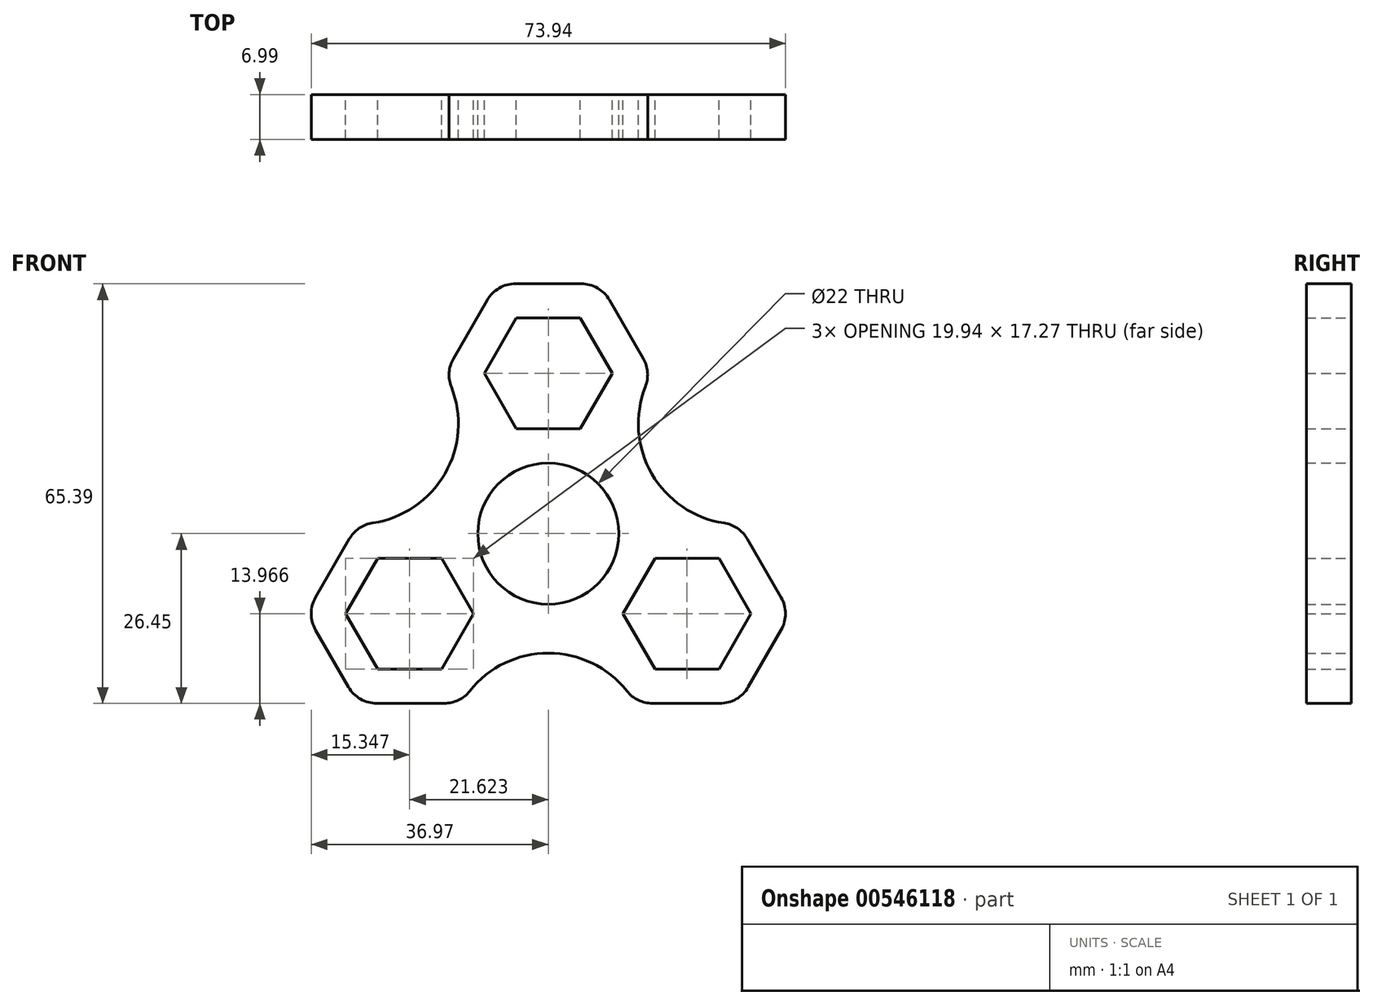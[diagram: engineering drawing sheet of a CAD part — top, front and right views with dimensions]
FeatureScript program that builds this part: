
annotation { "Feature Type Name" : "Feature", "Feature Type Description" : "" }
export const myFeature = defineFeature(function(context is Context, id is Id, definition is map)
    precondition{}
    {
        {
            var Q0;
            Q0=qCreatedBy(makeId("Front.planeOp"),FACE);
            var sketch = newSketch(context, id + "F0", { "sketchPlane" : qUnion([Q0])});
            skCircle(sketch, "E0", {"center": v(0, 0) * mm, "radius": 11 * mm});
            skCircle(sketch, "E1.cCircle", {"center": v(0, 0) * mm, "radius": 17.3 * mm, "construction": true});
            skLineSegment(sketch, "E1.0", {"start": v(-9.99, 17.3) * mm, "end": v(9.99, 17.3) * mm});
            skLineSegment(sketch, "E1.1", {"start": v(9.99, 17.3) * mm, "end": v(19.98, 0) * mm});
            skLineSegment(sketch, "E1.2", {"start": v(19.98, 0) * mm, "end": v(9.99, -17.3) * mm});
            skLineSegment(sketch, "E1.3", {"start": v(9.99, -17.3) * mm, "end": v(-9.99, -17.3) * mm});
            skLineSegment(sketch, "E1.4", {"start": v(-9.99, -17.3) * mm, "end": v(-19.98, 0) * mm});
            skLineSegment(sketch, "E1.5", {"start": v(-19.98, 0) * mm, "end": v(-9.99, 17.3) * mm});
            skPoint(sketch, "E1.0.midPoint", {"position": v(0, 17.3) * mm});
            skCircle(sketch, "E2.cCircle", {"center": v(0, 24.97) * mm, "radius": 13.97 * mm, "construction": true});
            skLineSegment(sketch, "E2.0", {"start": v(8.07, 11) * mm, "end": v(-8.07, 11) * mm});
            skLineSegment(sketch, "E2.1", {"start": v(-8.07, 11) * mm, "end": v(-16.13, 24.97) * mm});
            skLineSegment(sketch, "E2.2", {"start": v(-16.13, 24.97) * mm, "end": v(-8.07, 38.94) * mm});
            skLineSegment(sketch, "E2.3", {"start": v(-8.07, 38.94) * mm, "end": v(8.07, 38.94) * mm});
            skLineSegment(sketch, "E2.4", {"start": v(8.07, 38.94) * mm, "end": v(16.13, 24.97) * mm});
            skLineSegment(sketch, "E2.5", {"start": v(16.13, 24.97) * mm, "end": v(8.07, 11) * mm});
            skPoint(sketch, "E2.0.midPoint", {"position": v(0, 11) * mm});
            skCircle(sketch, "E3.cCircle", {"center": v(0, 24.97) * mm, "radius": 8.64 * mm, "construction": true});
            skLineSegment(sketch, "E3.0", {"start": v(-4.99, 33.6) * mm, "end": v(4.99, 33.6) * mm});
            skLineSegment(sketch, "E3.1", {"start": v(4.99, 33.6) * mm, "end": v(9.97, 24.97) * mm});
            skLineSegment(sketch, "E3.2", {"start": v(9.97, 24.97) * mm, "end": v(4.99, 16.33) * mm});
            skLineSegment(sketch, "E3.3", {"start": v(4.99, 16.33) * mm, "end": v(-4.99, 16.33) * mm});
            skLineSegment(sketch, "E3.4", {"start": v(-4.99, 16.33) * mm, "end": v(-9.97, 24.97) * mm});
            skLineSegment(sketch, "E3.5", {"start": v(-9.97, 24.97) * mm, "end": v(-4.99, 33.6) * mm});
            skPoint(sketch, "E3.0.midPoint", {"position": v(0, 33.6) * mm});
            skCircle(sketch, "E4.1.0", {"center": v(-21.62, -12.48) * mm, "radius": 13.97 * mm, "construction": true});
            skCircle(sketch, "E4.1.1", {"center": v(-21.62, -12.48) * mm, "radius": 8.64 * mm, "construction": true});
            skLineSegment(sketch, "E4.1.2", {"start": v(-16.64, -21.12) * mm, "end": v(-26.6, -21.12) * mm});
            skLineSegment(sketch, "E4.1.3", {"start": v(-13.56, -26.45) * mm, "end": v(-29.69, -26.45) * mm});
            skLineSegment(sketch, "E4.1.4", {"start": v(-29.69, -26.45) * mm, "end": v(-37.75, -12.48) * mm});
            skLineSegment(sketch, "E4.1.5", {"start": v(-13.56, 1.49) * mm, "end": v(-5.5, -12.48) * mm});
            skLineSegment(sketch, "E4.1.6", {"start": v(-16.64, -3.85) * mm, "end": v(-11.65, -12.48) * mm});
            skLineSegment(sketch, "E4.1.7", {"start": v(-11.65, -12.48) * mm, "end": v(-16.64, -21.12) * mm});
            skLineSegment(sketch, "E4.1.8", {"start": v(-26.6, -3.85) * mm, "end": v(-16.64, -3.85) * mm});
            skLineSegment(sketch, "E4.1.9", {"start": v(-31.6, -12.48) * mm, "end": v(-26.6, -3.85) * mm});
            skLineSegment(sketch, "E4.1.10", {"start": v(-29.69, 1.49) * mm, "end": v(-13.56, 1.49) * mm});
            skLineSegment(sketch, "E4.1.11", {"start": v(-37.75, -12.48) * mm, "end": v(-29.69, 1.49) * mm});
            skLineSegment(sketch, "E4.1.12", {"start": v(-5.5, -12.48) * mm, "end": v(-13.56, -26.45) * mm});
            skLineSegment(sketch, "E4.1.13", {"start": v(-26.6, -21.12) * mm, "end": v(-31.6, -12.48) * mm});
            skCircle(sketch, "E4.2.0", {"center": v(21.62, -12.48) * mm, "radius": 13.97 * mm, "construction": true});
            skCircle(sketch, "E4.2.1", {"center": v(21.62, -12.48) * mm, "radius": 8.64 * mm, "construction": true});
            skLineSegment(sketch, "E4.2.2", {"start": v(26.6, -3.85) * mm, "end": v(31.6, -12.48) * mm});
            skLineSegment(sketch, "E4.2.3", {"start": v(29.69, 1.49) * mm, "end": v(37.75, -12.48) * mm});
            skLineSegment(sketch, "E4.2.4", {"start": v(37.75, -12.48) * mm, "end": v(29.69, -26.45) * mm});
            skLineSegment(sketch, "E4.2.5", {"start": v(5.5, -12.48) * mm, "end": v(13.56, 1.49) * mm});
            skLineSegment(sketch, "E4.2.6", {"start": v(11.65, -12.48) * mm, "end": v(16.64, -3.85) * mm});
            skLineSegment(sketch, "E4.2.7", {"start": v(16.64, -3.85) * mm, "end": v(26.6, -3.85) * mm});
            skLineSegment(sketch, "E4.2.8", {"start": v(16.64, -21.12) * mm, "end": v(11.65, -12.48) * mm});
            skLineSegment(sketch, "E4.2.9", {"start": v(26.6, -21.12) * mm, "end": v(16.64, -21.12) * mm});
            skLineSegment(sketch, "E4.2.10", {"start": v(13.56, -26.45) * mm, "end": v(5.5, -12.48) * mm});
            skLineSegment(sketch, "E4.2.11", {"start": v(29.69, -26.45) * mm, "end": v(13.56, -26.45) * mm});
            skLineSegment(sketch, "E4.2.12", {"start": v(13.56, 1.49) * mm, "end": v(29.69, 1.49) * mm});
            skLineSegment(sketch, "E4.2.13", {"start": v(31.6, -12.48) * mm, "end": v(26.6, -21.12) * mm});
            skArc(sketch, "E5", {"start": v(-29.69, 1.49) * mm, "mid": v(-16.13, 9.31) * mm, "end": v(-16.13, 24.97) * mm});
            skArc(sketch, "E6", {"start": v(13.56, -26.45) * mm, "mid": v(0, -18.63) * mm, "end": v(-13.56, -26.45) * mm});
            skArc(sketch, "E7", {"start": v(16.13, 24.97) * mm, "mid": v(16.13, 9.31) * mm, "end": v(29.69, 1.49) * mm});
            skSolve(sketch);
        }
        {
            var Q0;
            Q0 = qSketchRegion(id + "F0", true);
            var Q1;
            {var subQ1=sQuery(id+"F0.wireOp",EDGE,"E2.0");var subQ7=sQuery(id+"F0.wireOp",EDGE,"E0");var subQ8=makeQuery(id+"F0.imprint","INTERSECT",VERTEX,{"derivedFrom":[subQ7,subQ1]});Q1=makeQuery(id+"F0.imprint","IMPRINT",FACE,{"disambiguationData":[TD([[makeQuery(id+"F0.imprint","IMPRINT",EDGE,{"disambiguationData":[TD([[subQ8,1.0]])],"derivedFrom":subQ7}),-1.0]])]});}
            var Q2;
            {var subQ1=sQuery(id+"F0.wireOp",EDGE,"E4.1.6");Q2=makeQuery(id+"F0.imprint","IMPRINT",FACE,{"disambiguationData":[TD([[makeQuery(id+"F0.imprint","IMPRINT",EDGE,{"derivedFrom":subQ1}),1.0]])]});}
            var Q3;
            {var subQ5=sQuery(id+"F0.wireOp",EDGE,"E0");var subQ7=sQuery(id+"F0.wireOp",EDGE,"E4.1.5");var subQ8=makeQuery(id+"F0.imprint","INTERSECT",VERTEX,{"derivedFrom":[subQ5,subQ7]});Q3=makeQuery(id+"F0.imprint","IMPRINT",FACE,{"disambiguationData":[TD([[makeQuery(id+"F0.imprint","IMPRINT",EDGE,{"disambiguationData":[TD([[subQ8,1.0]])],"derivedFrom":subQ5}),-1.0]])]});}
            var Q4;
            {var subQ1=sQuery(id+"F0.wireOp",EDGE,"E4.2.6");Q4=makeQuery(id+"F0.imprint","IMPRINT",FACE,{"disambiguationData":[TD([[makeQuery(id+"F0.imprint","IMPRINT",EDGE,{"derivedFrom":subQ1}),1.0]])]});}
            var Q5;
            {var subQ7=sQuery(id+"F0.wireOp",EDGE,"E3.3");Q5=makeQuery(id+"F0.imprint","IMPRINT",FACE,{"disambiguationData":[TD([[makeQuery(id+"F0.imprint","IMPRINT",EDGE,{"derivedFrom":subQ7}),1.0]])]});}
            var Q6;
            {var subQ1=sQuery(id+"F0.wireOp",EDGE,"E4.1.5");var subQ5=sQuery(id+"F0.wireOp",EDGE,"E0");var subQ6=makeQuery(id+"F0.imprint","INTERSECT",VERTEX,{"derivedFrom":[subQ5,subQ1]});Q6=makeQuery(id+"F0.imprint","IMPRINT",FACE,{"disambiguationData":[TD([[makeQuery(id+"F0.imprint","IMPRINT",EDGE,{"disambiguationData":[TD([[subQ6,-1.0]])],"derivedFrom":subQ5}),-1.0]])]});}
            extrude(context, id + "F1", {"entities" : qUnion([Q0, Q1, Q2, Q3, Q4, Q5, Q6]), "depth" : 7 * mm, "offsetDistance" : 25.4 * mm});
        }
        {
            var Q0;
            Q0=makeQuery(id+"F1.opExtrude","SWEPT_EDGE",EDGE,{"disambiguationData":[OSD([sQuery(id+"F0.wireOp",EDGE,"E2.4"),sQuery(id+"F0.wireOp",EDGE,"E2.5"),sQuery(id+"F0.wireOp",EDGE,"E7")])]});
            var Q1;
            Q1=makeQuery(id+"F1.opExtrude","SWEPT_EDGE",EDGE,{"disambiguationData":[OSD([sQuery(id+"F0.wireOp",EDGE,"E2.2"),sQuery(id+"F0.wireOp",EDGE,"E2.3")])]});
            var Q2;
            Q2=makeQuery(id+"F1.opExtrude","SWEPT_EDGE",EDGE,{"disambiguationData":[OSD([sQuery(id+"F0.wireOp",EDGE,"E2.3"),sQuery(id+"F0.wireOp",EDGE,"E2.4")])]});
            var Q3;
            Q3=makeQuery(id+"F1.opExtrude","SWEPT_EDGE",EDGE,{"disambiguationData":[OSD([sQuery(id+"F0.wireOp",EDGE,"E2.1"),sQuery(id+"F0.wireOp",EDGE,"E2.2"),sQuery(id+"F0.wireOp",EDGE,"E5")])]});
            var Q4;
            Q4=makeQuery(id+"F1.opExtrude","SWEPT_EDGE",EDGE,{"disambiguationData":[OSD([sQuery(id+"F0.wireOp",EDGE,"E4.1.10"),sQuery(id+"F0.wireOp",EDGE,"E4.1.11"),sQuery(id+"F0.wireOp",EDGE,"E5")])]});
            var Q5;
            Q5=makeQuery(id+"F1.opExtrude","SWEPT_EDGE",EDGE,{"disambiguationData":[OSD([sQuery(id+"F0.wireOp",EDGE,"E4.1.4"),sQuery(id+"F0.wireOp",EDGE,"E4.1.11")])]});
            var Q6;
            Q6=makeQuery(id+"F1.opExtrude","SWEPT_EDGE",EDGE,{"disambiguationData":[OSD([sQuery(id+"F0.wireOp",EDGE,"E4.1.3"),sQuery(id+"F0.wireOp",EDGE,"E4.1.12"),sQuery(id+"F0.wireOp",EDGE,"E6")])]});
            var Q7;
            Q7=makeQuery(id+"F1.opExtrude","SWEPT_EDGE",EDGE,{"disambiguationData":[OSD([sQuery(id+"F0.wireOp",EDGE,"E4.1.3"),sQuery(id+"F0.wireOp",EDGE,"E4.1.4")])]});
            var Q8;
            Q8=makeQuery(id+"F1.opExtrude","SWEPT_EDGE",EDGE,{"disambiguationData":[OSD([sQuery(id+"F0.wireOp",EDGE,"E4.2.10"),sQuery(id+"F0.wireOp",EDGE,"E4.2.11"),sQuery(id+"F0.wireOp",EDGE,"E6")])]});
            var Q9;
            Q9=makeQuery(id+"F1.opExtrude","SWEPT_EDGE",EDGE,{"disambiguationData":[OSD([sQuery(id+"F0.wireOp",EDGE,"E4.2.4"),sQuery(id+"F0.wireOp",EDGE,"E4.2.11")])]});
            var Q10;
            Q10=makeQuery(id+"F1.opExtrude","SWEPT_EDGE",EDGE,{"disambiguationData":[OSD([sQuery(id+"F0.wireOp",EDGE,"E4.2.3"),sQuery(id+"F0.wireOp",EDGE,"E4.2.4")])]});
            var Q11;
            Q11=makeQuery(id+"F1.opExtrude","SWEPT_EDGE",EDGE,{"disambiguationData":[OSD([sQuery(id+"F0.wireOp",EDGE,"E4.2.3"),sQuery(id+"F0.wireOp",EDGE,"E4.2.12"),sQuery(id+"F0.wireOp",EDGE,"E7")])]});
            fillet(context, id + "F2", {"entities" : qUnion([Q0, Q1, Q2, Q3, Q4, Q5, Q6, Q7, Q8, Q9, Q10, Q11]), "radius" : 5.08 * mm, "tangentPropagation" : true, "allowEdgeOverflow" : false});
        }
    });
